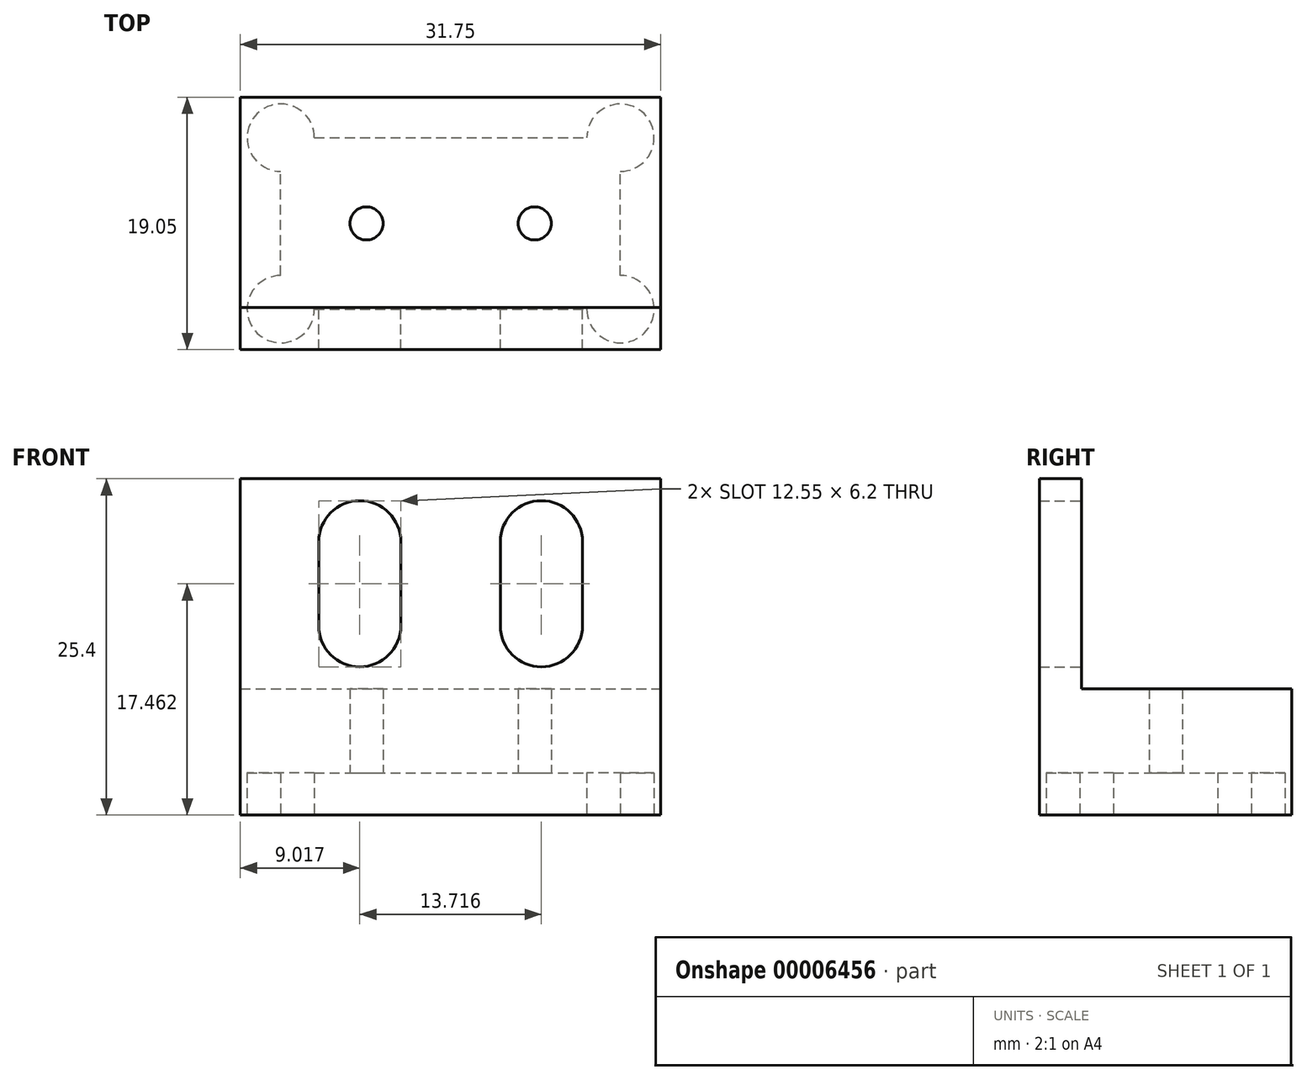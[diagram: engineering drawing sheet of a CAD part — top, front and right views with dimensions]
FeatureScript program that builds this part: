
annotation { "Feature Type Name" : "Feature", "Feature Type Description" : "" }
export const myFeature = defineFeature(function(context is Context, id is Id, definition is map)
    precondition{}
    {
        {
            var Q0;
            Q0=qCreatedBy(makeId("Top.planeOp"),FACE);
            var sketch = newSketch(context, id + "F0", { "sketchPlane" : qUnion([Q0])});
            skLineSegment(sketch, "E0.bottom", {"start": v(0, 0) * mm, "end": v(31.75, 0) * mm});
            skLineSegment(sketch, "E0.top", {"start": v(0, 19.05) * mm, "end": v(31.75, 19.05) * mm});
            skLineSegment(sketch, "E0.left", {"start": v(0, 0) * mm, "end": v(0, 19.05) * mm});
            skLineSegment(sketch, "E0.right", {"start": v(31.75, 0) * mm, "end": v(31.75, 19.05) * mm});
            skSolve(sketch);
        }
        {
            var Q0;
            Q0=makeQuery(id+"F0.imprint","IMPRINT",FACE,{"disambiguationData":[TD([[makeQuery(id+"F0.imprint","IMPRINT",EDGE,{"derivedFrom":sQuery(id+"F0.wireOp",EDGE,"E0.bottom")}),1.0]])]});
            extrude(context, id + "F1", {"entities" : qUnion([Q0]), "depth" : 9.52 * mm});
        }
        {
            var Q0;
            Q0=makeQuery(id+"F1.opExtrude","CAP_FACE",FACE,{"disambiguationData":[OSD([sQuery(id+"F0.wireOp",EDGE,"E0.bottom"),sQuery(id+"F0.wireOp",EDGE,"E0.top"),sQuery(id+"F0.wireOp",EDGE,"E0.left"),sQuery(id+"F0.wireOp",EDGE,"E0.right")])],"isStart":true});
            var sketch = newSketch(context, id + "F2", { "sketchPlane" : qUnion([Q0])});
            skLineSegment(sketch, "E1.bottom", {"start": v(5.59, -3.05) * mm, "end": v(26.16, -3.05) * mm});
            skLineSegment(sketch, "E1.top", {"start": v(5.59, -16) * mm, "end": v(26.16, -16) * mm});
            skLineSegment(sketch, "E1.left", {"start": v(3.05, -5.59) * mm, "end": v(3.05, -13.46) * mm});
            skLineSegment(sketch, "E1.right", {"start": v(28.7, -5.59) * mm, "end": v(28.7, -13.46) * mm});
            skArc(sketch, "E2", {"start": v(5.59, -3.05) * mm, "mid": v(1.25, -1.25) * mm, "end": v(3.05, -5.59) * mm});
            skArc(sketch, "E3", {"start": v(28.7, -5.59) * mm, "mid": v(30.5, -1.25) * mm, "end": v(26.16, -3.05) * mm});
            skArc(sketch, "E4", {"start": v(26.16, -16) * mm, "mid": v(30.5, -17.8) * mm, "end": v(28.7, -13.46) * mm});
            skArc(sketch, "E5", {"start": v(3.05, -13.46) * mm, "mid": v(1.25, -17.8) * mm, "end": v(5.59, -16) * mm});
            skSolve(sketch);
        }
        {
            var Q0;
            Q0 = qSketchRegion(id + "F2", true);
            extrude(context, id + "F3", {"entities" : qUnion([Q0]), "operationType" : NewBodyOperationType.REMOVE, "oppositeDirection" : true, "depth" : 3.17 * mm});
        }
        {
            var Q0;
            Q0=makeQuery(id+"F3.boolean.opBoolean","COPY",FACE,{"derivedFrom":makeQuery(id+"F3.opExtrude","CAP_FACE",FACE,{"disambiguationData":[OSD([sQuery(id+"F2.wireOp",EDGE,"E1.bottom"),sQuery(id+"F2.wireOp",EDGE,"E1.top"),sQuery(id+"F2.wireOp",EDGE,"E1.left"),sQuery(id+"F2.wireOp",EDGE,"E1.right"),sQuery(id+"F2.wireOp",EDGE,"E2"),sQuery(id+"F2.wireOp",EDGE,"E3"),sQuery(id+"F2.wireOp",EDGE,"E4"),sQuery(id+"F2.wireOp",EDGE,"E5")])],"isStart":false})});
            var sketch = newSketch(context, id + "F4", { "sketchPlane" : qUnion([Q0])});
            skCircle(sketch, "E6", {"center": v(9.53, -9.53) * mm, "radius": 1.25 * mm});
            skCircle(sketch, "E7", {"center": v(22.23, -9.53) * mm, "radius": 1.25 * mm});
            skLineSegment(sketch, "E8", {"start": v(28.7, -9.53) * mm, "end": v(22.23, -9.53) * mm, "construction": true});
            skLineSegment(sketch, "E9", {"start": v(9.53, -9.53) * mm, "end": v(3.05, -9.53) * mm, "construction": true});
            skSolve(sketch);
        }
        {
            var Q0;
            Q0 = qSketchRegion(id + "F4", true);
            extrude(context, id + "F5", {"entities" : qUnion([Q0]), "operationType" : NewBodyOperationType.REMOVE, "endBound" : BoundingType.UP_TO_NEXT, "oppositeDirection" : true, "depth" : 25.4 * mm});
        }
        {
            var Q0;
            Q0=makeQuery(id+"F1.opExtrude","CAP_FACE",FACE,{"disambiguationData":[OSD([sQuery(id+"F0.wireOp",EDGE,"E0.bottom"),sQuery(id+"F0.wireOp",EDGE,"E0.top"),sQuery(id+"F0.wireOp",EDGE,"E0.left"),sQuery(id+"F0.wireOp",EDGE,"E0.right")])],"isStart":false});
            var sketch = newSketch(context, id + "F6", { "sketchPlane" : qUnion([Q0])});
            skLineSegment(sketch, "E10.bottom", {"start": v(0, 0) * mm, "end": v(31.75, 0) * mm});
            skLineSegment(sketch, "E10.top", {"start": v(0, 3.18) * mm, "end": v(31.75, 3.18) * mm});
            skLineSegment(sketch, "E10.left", {"start": v(0, 0) * mm, "end": v(0, 3.18) * mm});
            skLineSegment(sketch, "E10.right", {"start": v(31.75, 0) * mm, "end": v(31.75, 3.18) * mm});
            skSolve(sketch);
        }
        {
            var Q0;
            Q0 = qSketchRegion(id + "F6", true);
            extrude(context, id + "F7", {"entities" : qUnion([Q0]), "operationType" : NewBodyOperationType.ADD, "depth" : 22.22 * mm - 6.35 * mm});
        }
        {
            var Q0;
            Q0=makeQuery(id+"F7.opExtrude","SWEPT_FACE",FACE,{"disambiguationData":[OSD([sQuery(id+"F6.wireOp",EDGE,"E10.top")])]});
            var sketch = newSketch(context, id + "F8", { "sketchPlane" : qUnion([Q0])});
            skArc(sketch, "E11", {"start": v(-19.63, 20.64) * mm, "mid": v(-22.73, 23.74) * mm, "end": v(-25.83, 20.64) * mm});
            skArc(sketch, "E12", {"start": v(-25.83, 14.29) * mm, "mid": v(-22.73, 11.19) * mm, "end": v(-19.63, 14.29) * mm});
            skArc(sketch, "E13", {"start": v(-12.12, 14.29) * mm, "mid": v(-9.02, 11.19) * mm, "end": v(-5.92, 14.29) * mm});
            skArc(sketch, "E14", {"start": v(-5.92, 20.64) * mm, "mid": v(-9.02, 23.74) * mm, "end": v(-12.12, 20.64) * mm});
            skLineSegment(sketch, "E15", {"start": v(-22.73, 20.64) * mm, "end": v(-31.75, 20.64) * mm, "construction": true});
            skLineSegment(sketch, "E16", {"start": v(-9.02, 20.64) * mm, "end": v(0, 20.64) * mm, "construction": true});
            skLineSegment(sketch, "E17", {"start": v(-19.63, 20.64) * mm, "end": v(-19.63, 14.29) * mm});
            skLineSegment(sketch, "E18", {"start": v(-25.83, 20.64) * mm, "end": v(-25.83, 14.29) * mm});
            skLineSegment(sketch, "E19", {"start": v(-12.12, 14.29) * mm, "end": v(-12.12, 20.64) * mm});
            skLineSegment(sketch, "E20", {"start": v(-5.92, 20.64) * mm, "end": v(-5.92, 14.29) * mm});
            skSolve(sketch);
        }
        {
            var Q0;
            Q0 = qSketchRegion(id + "F8", true);
            extrude(context, id + "F9", {"entities" : qUnion([Q0]), "operationType" : NewBodyOperationType.REMOVE, "endBound" : BoundingType.THROUGH_ALL, "oppositeDirection" : true, "depth" : 25.4 * mm});
        }
    });
